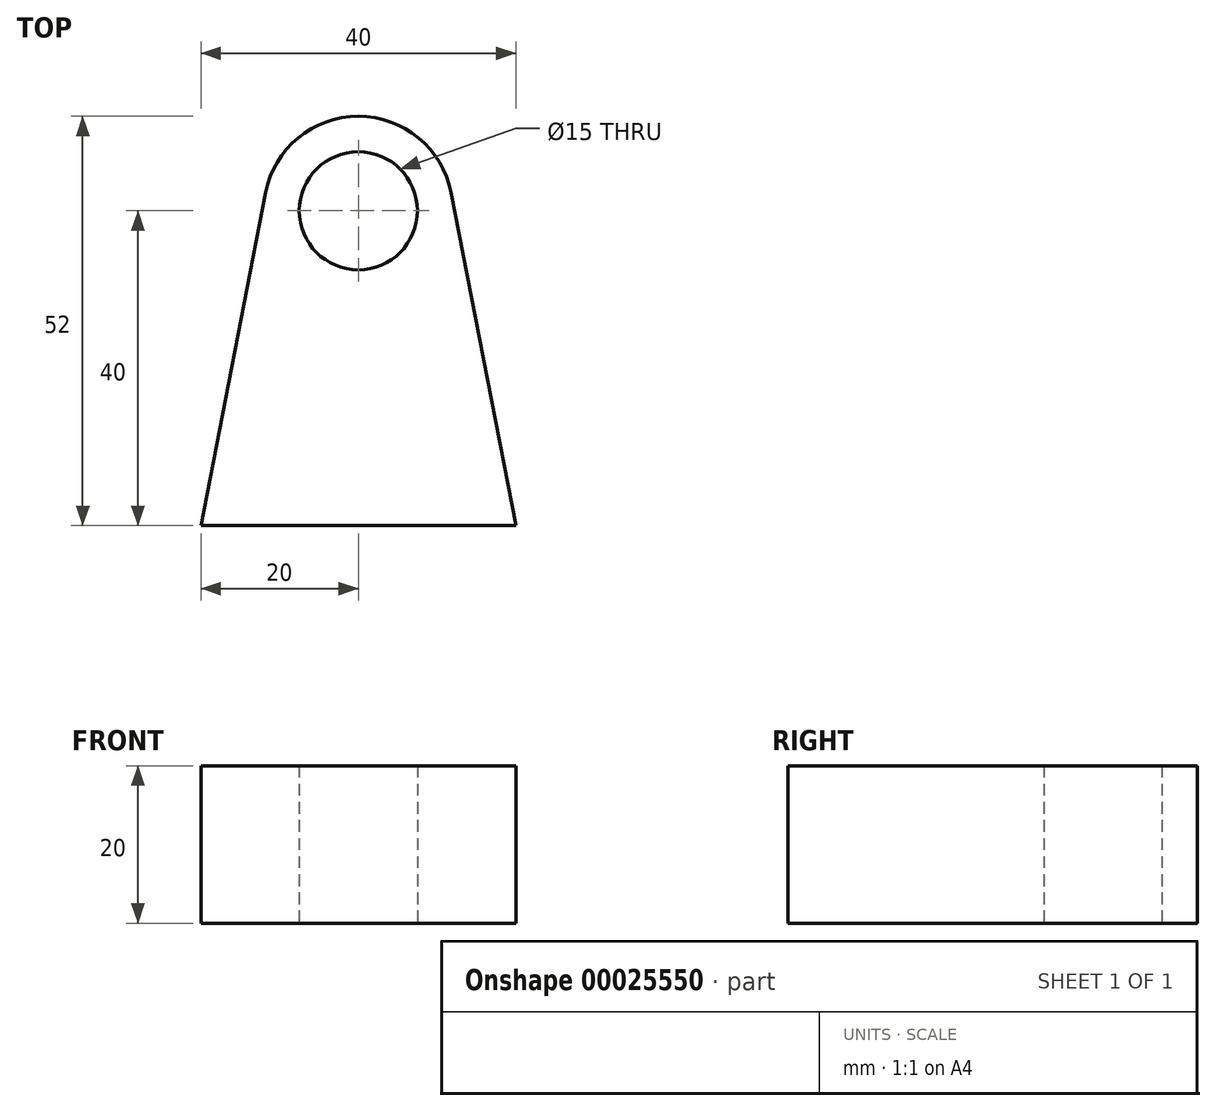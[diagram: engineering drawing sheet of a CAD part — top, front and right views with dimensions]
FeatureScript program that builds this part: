
annotation { "Feature Type Name" : "Feature", "Feature Type Description" : "" }
export const myFeature = defineFeature(function(context is Context, id is Id, definition is map)
    precondition{}
    {
        {
            var Q0;
            Q0=qCreatedBy(makeId("Top.planeOp"),FACE);
            var sketch = newSketch(context, id + "F0", { "sketchPlane" : qUnion([Q0])});
            skArc(sketch, "E0", {"start": v(11.78, 42.29) * mm, "mid": v(0, 52) * mm, "end": v(-11.78, 42.29) * mm});
            skLineSegment(sketch, "E1", {"start": v(-11.78, 42.29) * mm, "end": v(-20, 0) * mm});
            skLineSegment(sketch, "E2", {"start": v(-20, 0) * mm, "end": v(20, 0) * mm});
            skLineSegment(sketch, "E3", {"start": v(20, 0) * mm, "end": v(11.78, 42.29) * mm});
            skPoint(sketch, "E4", {"position": v(0, 0) * mm});
            skCircle(sketch, "E5", {"center": v(0, 40) * mm, "radius": 7.5 * mm});
            skSolve(sketch);
        }
        {
            var Q0;
            Q0 = qSketchRegion(id + "F0", true);
            extrude(context, id + "F1", {"entities" : qUnion([Q0]), "depth" : 20 * mm});
        }
    });
